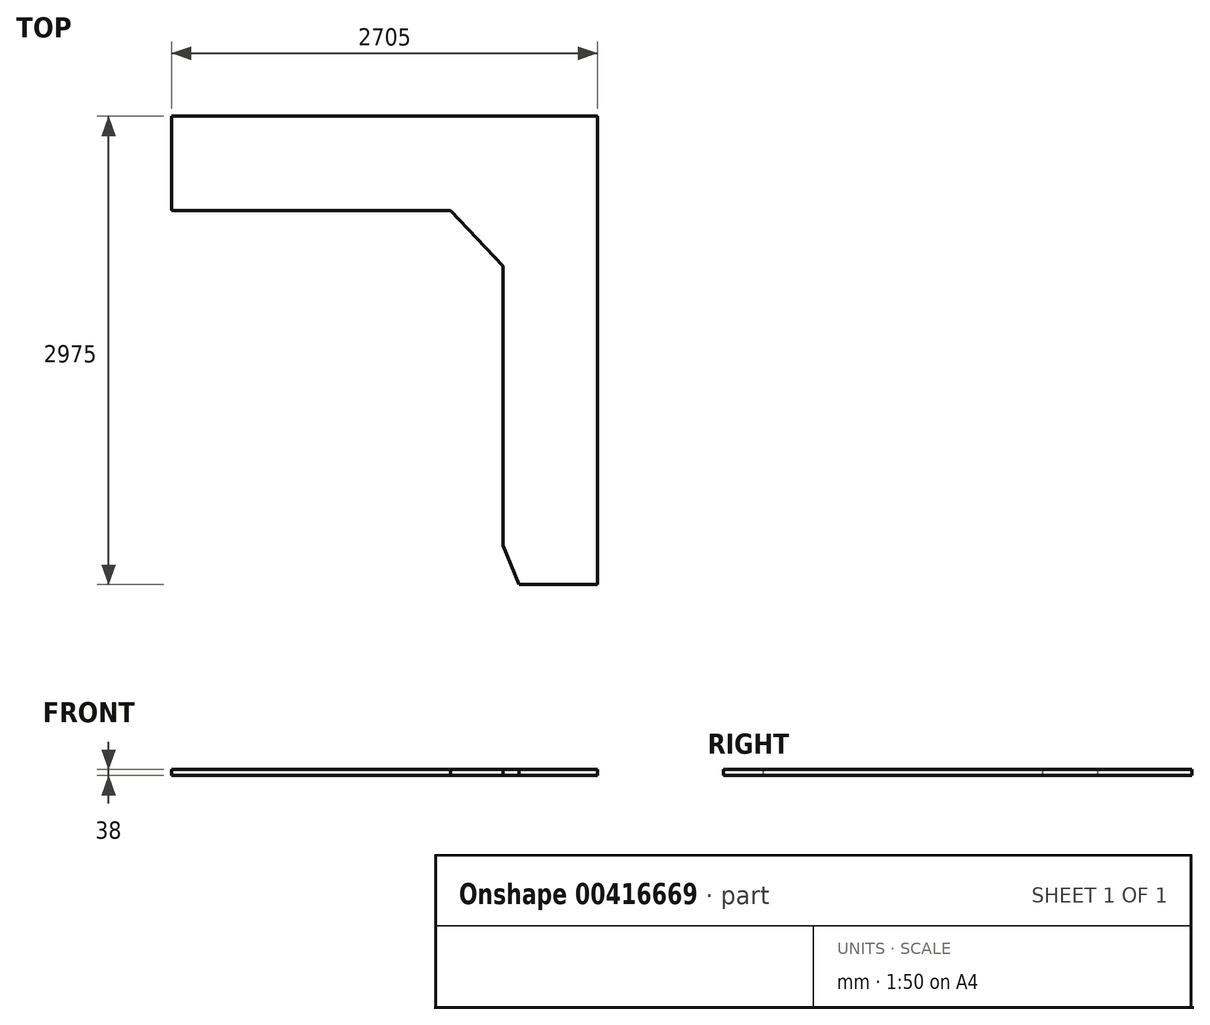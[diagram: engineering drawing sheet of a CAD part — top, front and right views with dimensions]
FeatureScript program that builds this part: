
annotation { "Feature Type Name" : "Feature", "Feature Type Description" : "" }
export const myFeature = defineFeature(function(context is Context, id is Id, definition is map)
    precondition{}
    {
        {
            var Q0;
            Q0=qCreatedBy(makeId("Top.planeOp"),FACE);
            var sketch = newSketch(context, id + "F0", { "sketchPlane" : qUnion([Q0])});
            skLineSegment(sketch, "E0", {"start": v(-1128.42, 925.82) * mm, "end": v(1576.58, 925.82) * mm});
            skLineSegment(sketch, "E1", {"start": v(1576.58, 925.82) * mm, "end": v(1576.58, -2049.18) * mm});
            skLineSegment(sketch, "E2", {"start": v(1576.58, -2049.18) * mm, "end": v(1076.58, -2049.18) * mm});
            skLineSegment(sketch, "E3", {"start": v(976.58, -1799.18) * mm, "end": v(976.58, -24.18) * mm});
            skLineSegment(sketch, "E4", {"start": v(976.58, -24.18) * mm, "end": v(641.58, 325.82) * mm});
            skLineSegment(sketch, "E5", {"start": v(641.58, 325.82) * mm, "end": v(-1128.42, 325.82) * mm});
            skLineSegment(sketch, "E6", {"start": v(-1128.42, 325.82) * mm, "end": v(-1128.42, 925.82) * mm});
            skLineSegment(sketch, "E7", {"start": v(976.58, -1799.18) * mm, "end": v(1076.58, -2049.18) * mm});
            skSolve(sketch);
        }
        {
            var Q0;
            Q0 = qSketchRegion(id + "F0", true);
            extrude(context, id + "F1", {"entities" : qUnion([Q0]), "depth" : 38 * mm});
        }
    });
